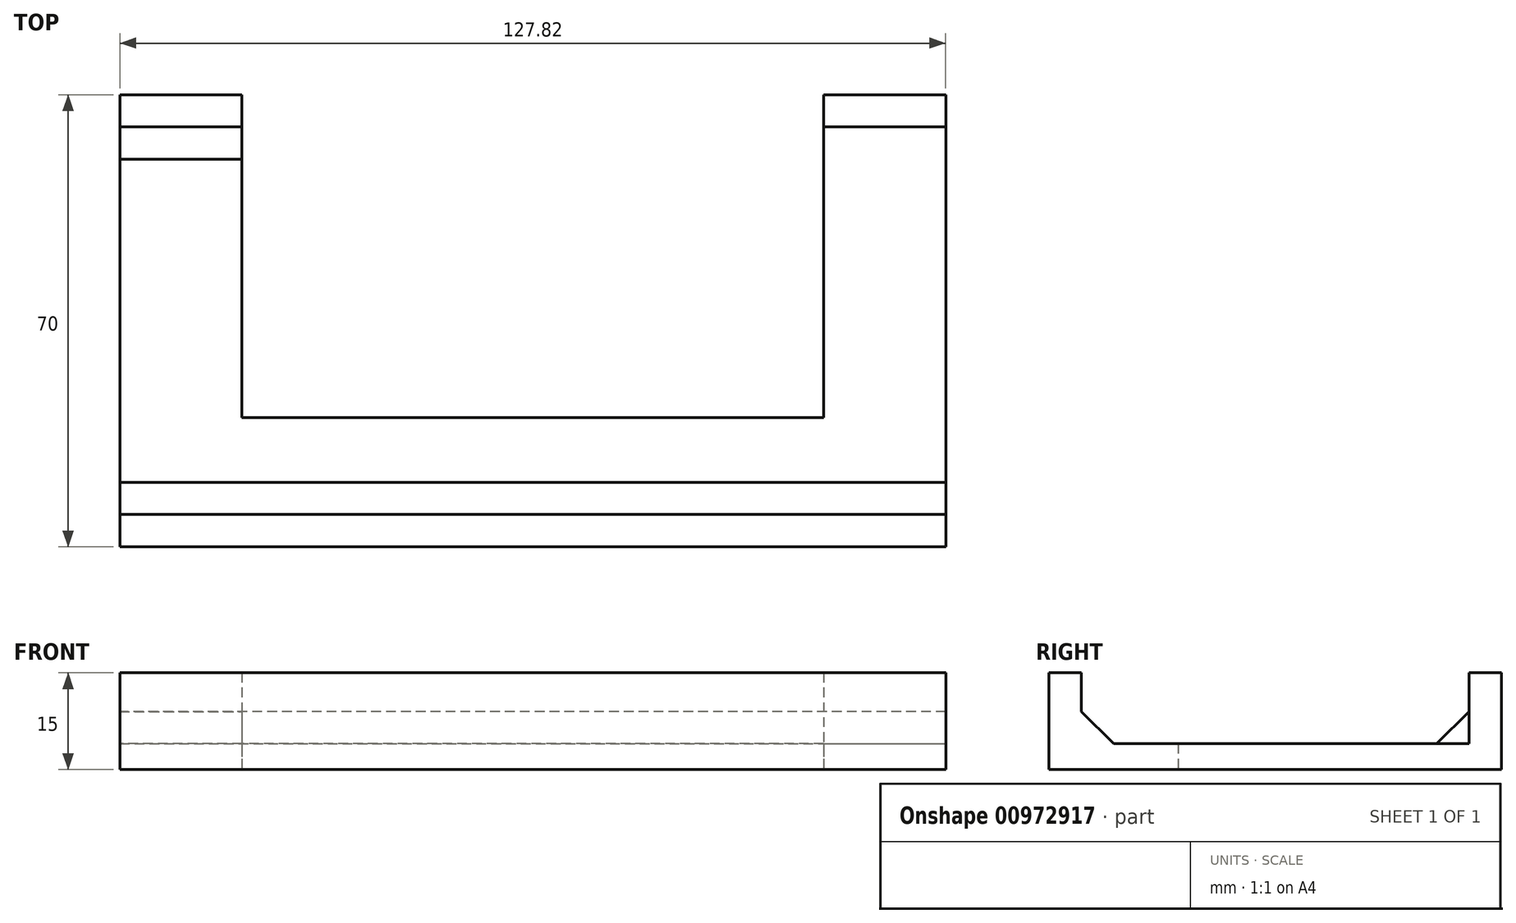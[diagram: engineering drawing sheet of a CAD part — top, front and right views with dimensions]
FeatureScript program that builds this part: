
annotation { "Feature Type Name" : "Feature", "Feature Type Description" : "" }
export const myFeature = defineFeature(function(context is Context, id is Id, definition is map)
    precondition{}
    {
        {
            var Q0;
            Q0=qCreatedBy(makeId("Top.planeOp"),FACE);
            var sketch = newSketch(context, id + "F0", { "sketchPlane" : qUnion([Q0])});
            skLineSegment(sketch, "E0", {"start": v(-44.02, 43.34) * mm, "end": v(-44.02, -26.66) * mm});
            skLineSegment(sketch, "E1", {"start": v(-44.02, -26.66) * mm, "end": v(83.8, -26.66) * mm});
            skLineSegment(sketch, "E2", {"start": v(83.8, -26.66) * mm, "end": v(83.8, 43.34) * mm});
            skLineSegment(sketch, "E3", {"start": v(83.8, 43.34) * mm, "end": v(64.9, 43.34) * mm});
            skLineSegment(sketch, "E4", {"start": v(64.9, 43.34) * mm, "end": v(64.9, -6.66) * mm});
            skLineSegment(sketch, "E5", {"start": v(64.9, -6.66) * mm, "end": v(-25.1, -6.66) * mm});
            skLineSegment(sketch, "E6", {"start": v(-25.1, -6.66) * mm, "end": v(-25.1, 43.34) * mm});
            skLineSegment(sketch, "E7", {"start": v(-25.1, 43.34) * mm, "end": v(-44.02, 43.34) * mm});
            skLineSegment(sketch, "E8", {"start": v(-44.02, -21.66) * mm, "end": v(83.8, -21.66) * mm});
            skLineSegment(sketch, "E9", {"start": v(-44.02, 38.34) * mm, "end": v(-25.1, 38.34) * mm});
            skLineSegment(sketch, "E10.trimOffspring", {"start": v(64.9, 38.34) * mm, "end": v(83.8, 38.34) * mm});
            skSolve(sketch);
        }
        {
            var Q0;
            {var subQ0=sQuery(id+"F0.wireOp",EDGE,"E5");Q0=makeQuery(id+"F0.imprint","IMPRINT",FACE,{"disambiguationData":[TD([[makeQuery(id+"F0.imprint","IMPRINT",EDGE,{"derivedFrom":subQ0}),1.0]])]});}
            var Q1;
            {var subQ0=sQuery(id+"F0.wireOp",EDGE,"E1");Q1=makeQuery(id+"F0.imprint","IMPRINT",FACE,{"disambiguationData":[TD([[makeQuery(id+"F0.imprint","IMPRINT",EDGE,{"derivedFrom":subQ0}),1.0]])]});}
            var Q2;
            {var subQ0=sQuery(id+"F0.wireOp",EDGE,"E7");Q2=makeQuery(id+"F0.imprint","IMPRINT",FACE,{"disambiguationData":[TD([[makeQuery(id+"F0.imprint","IMPRINT",EDGE,{"derivedFrom":subQ0}),1.0]])]});}
            extrude(context, id + "F1", {"entities" : qUnion([Q0, Q1, Q2]), "depth" : 4 * mm, "offsetDistance" : 25 * mm});
        }
        {
            var Q0;
            {var subQ0=sQuery(id+"F0.wireOp",EDGE,"E1");Q0=makeQuery(id+"F0.imprint","IMPRINT",FACE,{"disambiguationData":[TD([[makeQuery(id+"F0.imprint","IMPRINT",EDGE,{"derivedFrom":subQ0}),1.0]])]});}
            var Q1;
            {var subQ0=sQuery(id+"F0.wireOp",EDGE,"E7");Q1=makeQuery(id+"F0.imprint","IMPRINT",FACE,{"disambiguationData":[TD([[makeQuery(id+"F0.imprint","IMPRINT",EDGE,{"derivedFrom":subQ0}),1.0]])]});}
            var Q2;
            {var subQ0=sQuery(id+"F0.wireOp",EDGE,"E3");Q2=makeQuery(id+"F0.imprint","IMPRINT",FACE,{"disambiguationData":[TD([[makeQuery(id+"F0.imprint","IMPRINT",EDGE,{"derivedFrom":subQ0}),1.0]])]});}
            extrude(context, id + "F2", {"entities" : qUnion([Q0, Q1, Q2]), "operationType" : NewBodyOperationType.ADD, "depth" : 15 * mm, "offsetDistance" : 25 * mm});
        }
        {
            var Q0;
            Q0=makeQuery(id+"F2.boolean.opBoolean","INTERSECT",EDGE,{"derivedFrom":[makeQuery(id+"F1.opExtrude","CAP_FACE",FACE,{"disambiguationData":[OSD([sQuery(id+"F0.wireOp",EDGE,"E0"),sQuery(id+"F0.wireOp",EDGE,"E1"),sQuery(id+"F0.wireOp",EDGE,"E2"),sQuery(id+"F0.wireOp",EDGE,"E4"),sQuery(id+"F0.wireOp",EDGE,"E5"),sQuery(id+"F0.wireOp",EDGE,"E6"),sQuery(id+"F0.wireOp",EDGE,"E7"),sQuery(id+"F0.wireOp",EDGE,"E10.trimOffspring")])],"isStart":false}),makeQuery(id+"F2.opExtrude","SWEPT_FACE",FACE,{"disambiguationData":[OSD([sQuery(id+"F0.wireOp",EDGE,"E8")])]})]});
            var Q1;
            Q1=makeQuery(id+"F2.boolean.opBoolean","INTERSECT",EDGE,{"derivedFrom":[makeQuery(id+"F1.opExtrude","CAP_FACE",FACE,{"disambiguationData":[OSD([sQuery(id+"F0.wireOp",EDGE,"E0"),sQuery(id+"F0.wireOp",EDGE,"E1"),sQuery(id+"F0.wireOp",EDGE,"E2"),sQuery(id+"F0.wireOp",EDGE,"E4"),sQuery(id+"F0.wireOp",EDGE,"E5"),sQuery(id+"F0.wireOp",EDGE,"E6"),sQuery(id+"F0.wireOp",EDGE,"E7"),sQuery(id+"F0.wireOp",EDGE,"E10.trimOffspring")])],"isStart":false}),makeQuery(id+"F2.opExtrude","SWEPT_FACE",FACE,{"disambiguationData":[OSD([sQuery(id+"F0.wireOp",EDGE,"E9")])]})]});
            var Q2;
            Q2=makeQuery(id+"F1.opExtrude","CAP_EDGE",EDGE,{"disambiguationData":[OSD([sQuery(id+"F0.wireOp",EDGE,"E10.trimOffspring")])],"isStart":false});
            chamfer(context, id + "F3", {"entities" : qUnion([Q0, Q1, Q2]), "width" : 5 * mm, "tangentPropagation" : true});
        }
    });
